# Revit family: Bath-Drop_In-KOHLER-ARCHER-K-45592T_1
name_source: partatom
category: Plumbing Fixtures
revit_build: Autodesk Revit 2017 (Build: 20160225_1515(x64)
units: mm (PartAtom-declared; Revit-internal decimal feet)

## family parameters
Cut with Voids When Loaded = No
Host = Face
OmniClass Number = 23.31.15.00
OmniClass Title = Bathtubs
Part Type = Normal
Room Calculation Point = No
Round Connector Dimension = Use Diameter
Shared = No

## types (2) — shared parameters
ADA Compliant = No
Assembly Code = D2010500
CW Connection = No
Cold Water Inlet = Cold Water Inlet
Date Modified = 02/10/2021
Default Elevation = 0"
Drain Included = No
Finish = KOHLER-Enameled_Cast_Iron-0-White
HW Connection = No
Height = 18 5/16"
Hot Water Inlet = Hot Water Inlet
Length = 29 1/2"
Manufacturer = KOHLER Co.
Master Format 2014 = 22 41 19
Master Format 2014 Name = Residential Bathtubs
Material = Cast Iron
Product Documentation Link = https://files.kohler.com.cn
Product Name = ARCHER
Product Page URL = https://www.kohler.com.cn
URL = https://www.kohler.com.cn
Vent Connection = No
Waste Connection = Yes
Waste Water Outlet = Waste Water Outlet
WaterSense Certified = No
Width = 59 1/16"

## per-type parameters (varying)
| type | Description | Drain Location Distance | Left Hand Drain | Model | Right Hand Drain | Type |
| Left Hand Drain, 0-White | 1.5m built-in cast iron bathtub, L/DRAIN | 11 1/4" | Yes | K-45592T-GR1-0 | No | 1 |
| Right Hand Drain, 0-White | 1.5m built-in cast iron bathtub, R/DRAIN | 47 13/16" | No | K-45592T-GR2-0 | Yes | 2 |

## geometry (parser evidence)
native form markers: Sweep x5
no freeform markers — native parametric forms only
